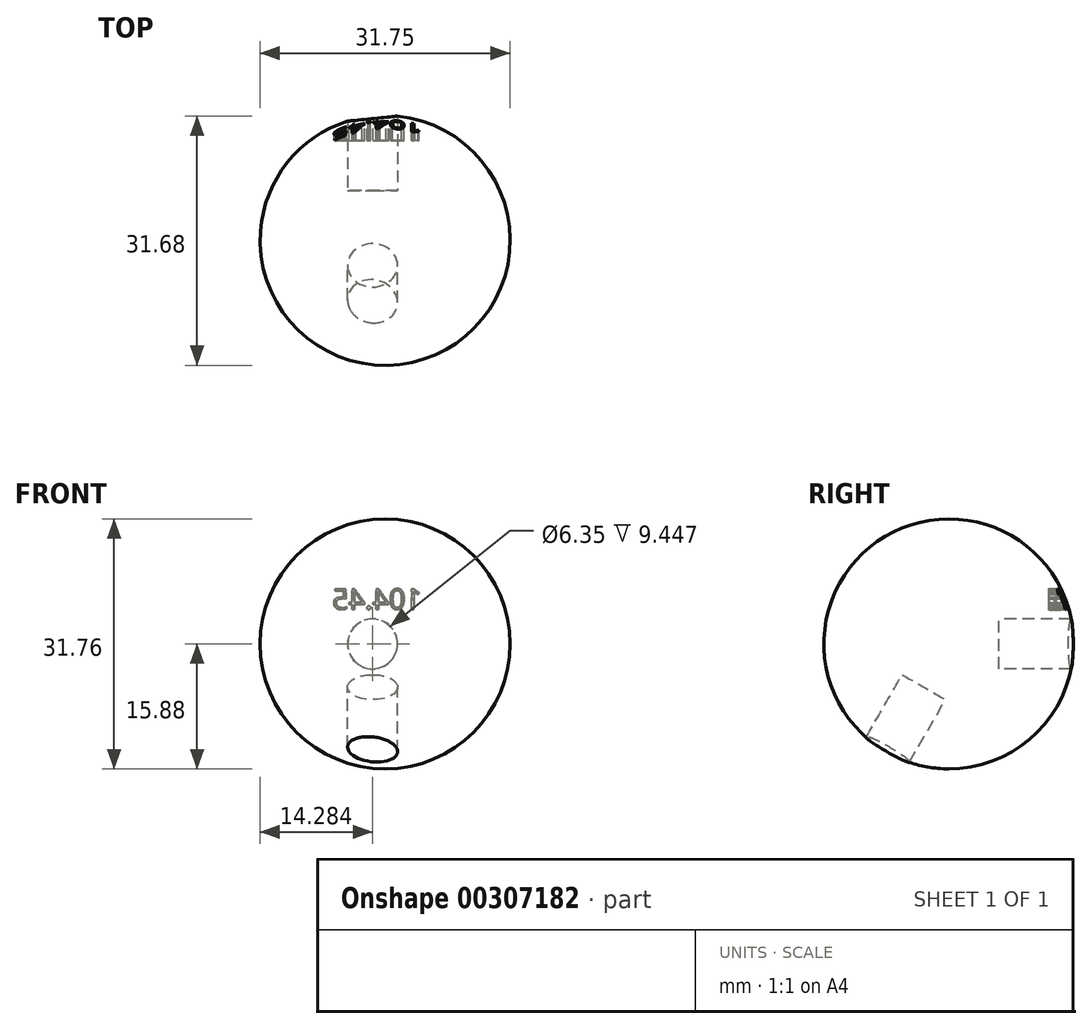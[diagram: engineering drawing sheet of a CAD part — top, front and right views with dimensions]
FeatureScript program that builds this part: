
annotation { "Feature Type Name" : "Feature", "Feature Type Description" : "" }
export const myFeature = defineFeature(function(context is Context, id is Id, definition is map)
    precondition{}
    {
        {
            var Q0;
            Q0=qCreatedBy(makeId("Top.planeOp"),FACE);
            var sketch = newSketch(context, id + "F0", { "sketchPlane" : qUnion([Q0])});
            skCircle(sketch, "E0", {"center": v(0, 0) * mm, "radius": 15.88 * mm});
            skSolve(sketch);
        }
        {
            var Q0;
            Q0=qCreatedBy(makeId("Front.planeOp"),FACE);
            var sketch = newSketch(context, id + "F1", { "sketchPlane" : qUnion([Q0])});
            skArc(sketch, "E1", {"start": v(0, 15.88) * mm, "mid": v(-15.88, 0) * mm, "end": v(0, -15.88) * mm});
            skLineSegment(sketch, "E2", {"start": v(0, -15.88) * mm, "end": v(0, 15.88) * mm});
            skSolve(sketch);
        }
        {
            var Q0;
            Q0=qSketchRegion(id+"F1",true);
            var Q1;
            Q1=sQuery(id+"F0.wireOp",EDGE,"E0");
            revolve(context, id + "F2", {"entities" : qUnion([Q0]), "axis" : qUnion([Q1]), "revolveType" : RevolveType.FULL});
        }
        {
            var Q0;
            Q0=qCreatedBy(makeId("Front.planeOp"),FACE);
            cPlane(context, id + "F3", {"entities" : qUnion([Q0]), "cplaneType" : CPlaneType.OFFSET, "offset" : 6.35 * mm, "oppositeDirection" : true, "width" : 152.4 * mm, "height" : 152.4 * mm});
        }
        {
            var Q0;
            Q0=qCreatedBy(id+"F3.planeOp",FACE);
            var sketch = newSketch(context, id + "F4", { "sketchPlane" : qUnion([Q0])});
            skCircle(sketch, "E3", {"center": v(-1.6, 0) * mm, "radius": 3.18 * mm});
            skSolve(sketch);
        }
        {
            var Q0;
            Q0=qSketchRegion(id+"F4",true);
            extrude(context, id + "F5", {"entities" : qUnion([Q0]), "oppositeDirection" : true, "depth" : 38.1 * mm});
        }
        {
            var Q0;
            Q0=makeQuery(id+"F5.opExtrude","CAP_FACE",FACE,{"disambiguationData":[OSD([sQuery(id+"F4.wireOp",EDGE,"E3")])],"isStart":false});
            var sketch = newSketch(context, id + "F6", { "sketchPlane" : qUnion([Q0])});
            skText(sketch, "E4", { "text": "104.45", "fontName": "OpenSans-Regular.ttf"});
            const initialGuessF6  = {"E4": [-0.00465, 0.00439, 1, 0, 0.00262]};
            skSetInitialGuess(sketch, initialGuessF6);
            skSolve(sketch);
        }
        {
            var Q0;
            Q0=qSketchRegion(id+"F6",true);
            extrude(context, id + "F7", {"entities" : qUnion([Q0]), "operationType" : NewBodyOperationType.REMOVE, "oppositeDirection" : true, "depth" : 31.75 * mm});
        }
        {
            var Q0;
            Q0=qCreatedBy(makeId("Front.planeOp"),FACE);
            var sketch = newSketch(context, id + "F8", { "sketchPlane" : qUnion([Q0])});
            skLineSegment(sketch, "E5", {"start": v(0, 0) * mm, "end": v(0, 31.16) * mm, "construction": true});
            skLineSegment(sketch, "E6", {"start": v(0, 0) * mm, "end": v(39.64, 0) * mm, "construction": true});
            skLineSegment(sketch, "E7", {"start": v(0, 0) * mm, "end": v(-35.4, 0) * mm, "construction": true});
            skSolve(sketch);
        }
        {
            var Q0;
            Q0=makeQuery(id+"F5.opExtrude","SWEPT_BODY",BODY,{"disambiguationData":[OSD([sQuery(id+"F4.wireOp",EDGE,"E3")])]});
            var Q1;
            Q1=sQuery(id+"F8.wireOp",EDGE,"E6");
            transform(context, id + "F9", {"entities" : qUnion([Q0]), "transformType" : TransformType.ROTATION, "transformAxis" : qUnion([Q1]), "angle" : 120 * degree, "oppositeDirection" : true, "makeCopy" : true});
        }
        {
            var Q0;
            Q0=makeQuery(id+"F9.opPattern","COPY",BODY,{"derivedFrom":makeQuery(id+"F5.opExtrude","SWEPT_BODY",BODY,{"disambiguationData":[OSD([sQuery(id+"F4.wireOp",EDGE,"E3")])]}),"instanceName":"1"});
            var Q1;
            Q1=makeQuery(id+"F5.opExtrude","SWEPT_BODY",BODY,{"disambiguationData":[OSD([sQuery(id+"F4.wireOp",EDGE,"E3")])]});
            var Q2;
            Q2=makeQuery(id+"F2.opRevolve","SWEPT_BODY",BODY,{"disambiguationData":[OSD([sQuery(id+"F1.wireOp",EDGE,"E1"),sQuery(id+"F1.wireOp",EDGE,"E2")])]});
            booleanBodies(context, id + "F10", {"operationType" : BooleanOperationType.SUBTRACTION, "tools" : qUnion([Q0, Q1]), "targets" : qUnion([Q2])});
        }
    });
